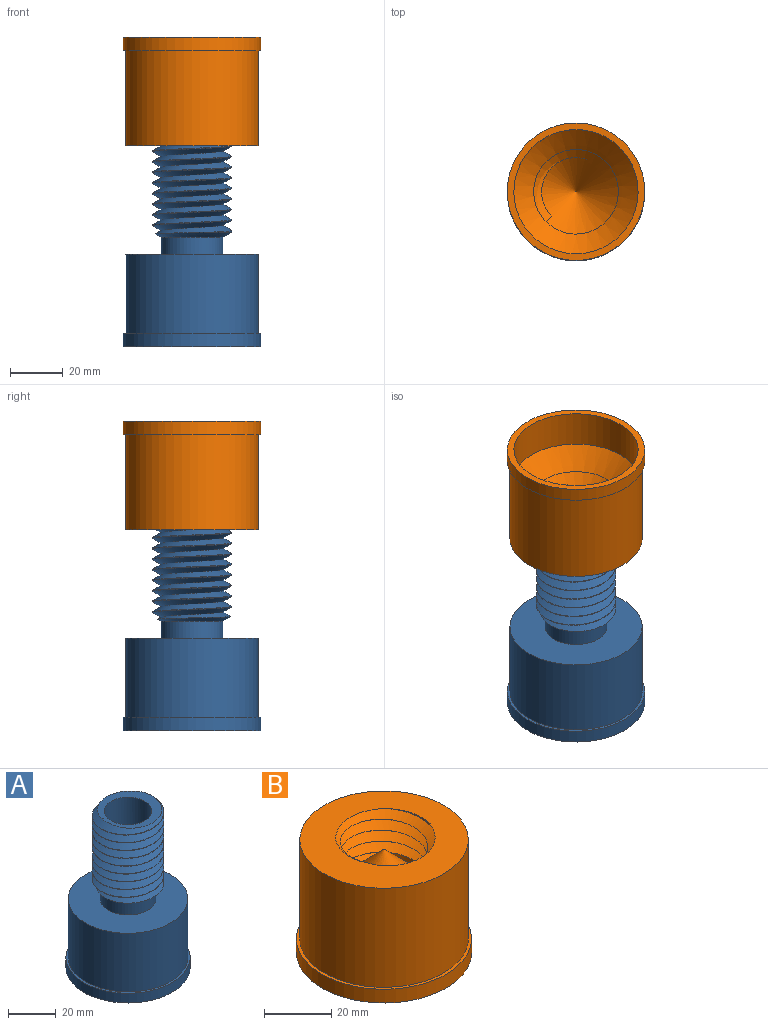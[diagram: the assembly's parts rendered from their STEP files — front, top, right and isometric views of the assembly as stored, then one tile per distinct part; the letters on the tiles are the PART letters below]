
ASSEMBLY  parts=2 mates=1
PART A: 15 faces, bbox 54.7x54.7x85.2 mm
  f0: cylinder r=26mm len=52mm, axis (0,0,-1), area 816.8mm2, adj f1,f2
  f1: plane 52x52mm, normal (0,0,1), area 160.2mm2, adj f0,f3
  f2: plane 52x52mm, normal (0,0,-1), area 388.8mm2, adj f0,f7
  f3: cylinder r=25mm len=50mm, axis (0,0,-1), area 4712.4mm2, adj f1,f4
  f4: plane 50x50mm, normal (0,0,1), area 1533.4mm2, adj f3,f10
  f5: cylinder r=10mm len=52.5mm, axis (0,0,-1), area 3298.7mm2, adj f6,f9
  f6: cone r=23.5mm half-angle=45deg, axis (0,0,-1), area 2009.3mm2, adj f5,f7
  f7: cylinder r=23.5mm len=47mm, axis (0,0,-1), area 2067.2mm2, adj f2,f6
  f8: cylinder r=15mm len=36.7mm, axis (0,0,-1), area 210.7mm2, adj f9,f11,f12,f13,f14
  f9: plane 29.68x29.62mm, normal (0,0,1), area 256.2mm2, adj f5,f8,f13,f14
  f10: cylinder r=11.7mm len=23.4mm, axis (0,0,-1), area 470.1mm2, adj f4,f11
  f11: cone r=15mm half-angle=60deg, axis (0,0,1), area 199.5mm2, adj f8,f10,f12,f14
  f12: plane 3.29x2.15mm, normal (0,1,0), area 1.5mm2, adj f8,f11,f13,f14
  f13: bspline ~40.57x34.64mm, area 2960mm2, adj f8,f9,f12,f14
  f14: bspline ~41.9x34.64mm, area 3010.4mm2, adj f8,f9,f11,f12,f13
PART B: 12 faces, bbox 54.1x54.1x45.3 mm
  f0: bspline ~36.95x32mm, area 1342.5mm2, adj f1,f2,f3,f10
  f1: plane 3.51x2.16mm, normal (0.71,-0.71,0), area 5.3mm2, adj f0,f2,f10
  f2: bspline ~36.95x32mm, area 1487.6mm2, adj f0,f1,f3,f10
  f3: plane 52.13x52.13mm, normal (0,0,1), area 1284.1mm2, adj f0,f2,f4,f10
  f4: cylinder r=25mm len=50mm, axis (0,0,-1), area 5654.9mm2, adj f3,f5
  f5: plane 52x52mm, normal (0,0,1), area 160.2mm2, adj f4,f6
  f6: cylinder r=26mm len=52mm, axis (0,0,-1), area 816.8mm2, adj f5,f7
  f7: plane 52x52mm, normal (0,0,-1), area 388.8mm2, adj f6,f8
  f8: cylinder r=23.5mm len=47mm, axis (0,0,-1), area 2067.2mm2, adj f7,f9
  f9: cone r=23.5mm half-angle=45deg, axis (0,0,-1), area 2453.6mm2, adj f8
  f10: cylinder r=16mm len=32mm, axis (0,0,-1), area 406.3mm2, adj f0,f1,f2,f3,f11
  f11: cone r=23.5mm half-angle=45deg, axis (0,0,-1), area 1137.4mm2, adj f10
PLACE A t=(-47.37,-1.14,-0.69)mm fixed
PLACE B rot(axis=(-0.71,0.71,0),180deg) t=(-47.37,-1.14,116.31)mm
MATE slider B.f9 <-> A.f0  axis (0,0,1) through (-47.37,-1.14,109.31)mm
